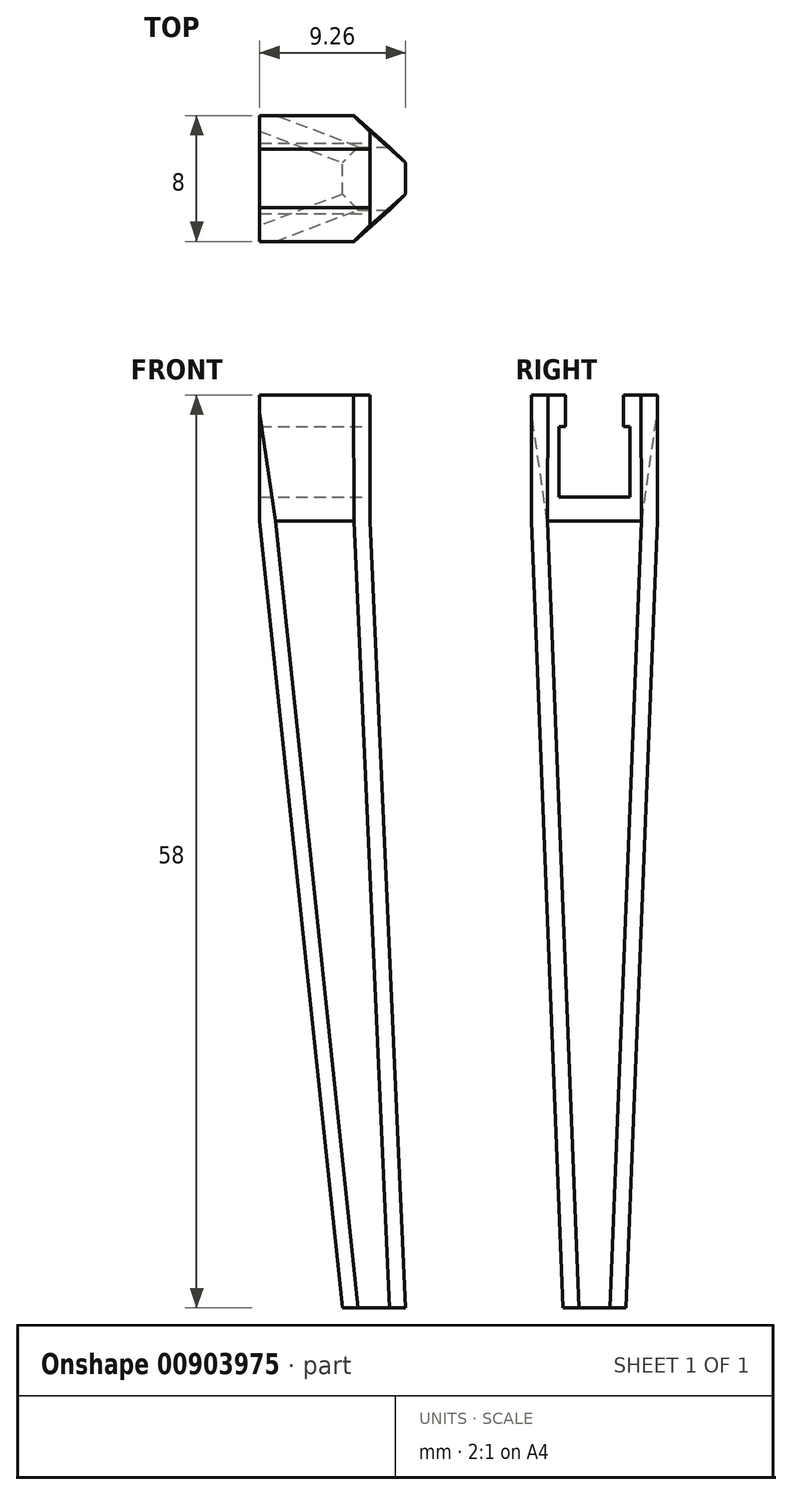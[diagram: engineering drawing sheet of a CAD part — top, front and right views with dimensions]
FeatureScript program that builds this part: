
annotation { "Feature Type Name" : "Feature", "Feature Type Description" : "" }
export const myFeature = defineFeature(function(context is Context, id is Id, definition is map)
    precondition{}
    {
        {
            var Q0;
            Q0=qCreatedBy(makeId("Front.planeOp"),FACE);
            var sketch = newSketch(context, id + "F0", { "sketchPlane" : qUnion([Q0])});
            skLineSegment(sketch, "E0", {"start": v(0, 0) * mm, "end": v(5.26, -50) * mm});
            skLineSegment(sketch, "E1", {"start": v(5.26, -50) * mm, "end": v(9.26, -50) * mm});
            skLineSegment(sketch, "E2", {"start": v(9.26, -50) * mm, "end": v(7, 0) * mm});
            skLineSegment(sketch, "E3", {"start": v(7, 0) * mm, "end": v(7, 8) * mm});
            skLineSegment(sketch, "E4", {"start": v(7, 8) * mm, "end": v(0, 8) * mm});
            skLineSegment(sketch, "E5", {"start": v(0, 8) * mm, "end": v(0, 0) * mm});
            skSolve(sketch);
        }
        {
            var Q0;
            Q0 = qSketchRegion(id + "F0", true);
            extrude(context, id + "F1", {"entities" : qUnion([Q0]), "endBound" : BoundingType.SYMMETRIC, "depth" : 8 * mm, "offsetDistance" : 25 * mm});
        }
        {
            var Q0;
            Q0=qCreatedBy(makeId("Right.planeOp"),FACE);
            var sketch = newSketch(context, id + "F2", { "sketchPlane" : qUnion([Q0])});
            skLineSegment(sketch, "E6", {"start": v(-2.25, 6) * mm, "end": v(-2.25, 1.5) * mm});
            skLineSegment(sketch, "E7", {"start": v(-2.25, 1.5) * mm, "end": v(2.25, 1.5) * mm});
            skLineSegment(sketch, "E8", {"start": v(2.25, 1.5) * mm, "end": v(2.25, 6) * mm});
            skLineSegment(sketch, "E9", {"start": v(2.25, 6) * mm, "end": v(1.85, 6) * mm});
            skLineSegment(sketch, "E10", {"start": v(1.85, 6) * mm, "end": v(1.85, 11) * mm});
            skLineSegment(sketch, "E11", {"start": v(1.85, 11) * mm, "end": v(-1.85, 11) * mm});
            skLineSegment(sketch, "E12", {"start": v(-1.85, 11) * mm, "end": v(-1.85, 6) * mm});
            skLineSegment(sketch, "E13", {"start": v(-1.85, 6) * mm, "end": v(-2.25, 6) * mm});
            skSolve(sketch);
        }
        {
            var Q0;
            Q0 = qSketchRegion(id + "F2", true);
            extrude(context, id + "F3", {"entities" : qUnion([Q0]), "operationType" : NewBodyOperationType.REMOVE, "endBound" : BoundingType.SYMMETRIC, "oppositeDirection" : true, "depth" : 25 * mm, "offsetDistance" : 25 * mm});
        }
        {
            var Q0;
            Q0=qCreatedBy(makeId("Right.planeOp"),FACE);
            var sketch = newSketch(context, id + "F4", { "sketchPlane" : qUnion([Q0])});
            skLineSegment(sketch, "E14", {"start": v(-4, 0) * mm, "end": v(-2, -50) * mm});
            skLineSegment(sketch, "E15", {"start": v(-2, -50) * mm, "end": v(-9.35, -50) * mm});
            skLineSegment(sketch, "E16", {"start": v(-9.35, -50) * mm, "end": v(-9.35, 0) * mm});
            skLineSegment(sketch, "E17", {"start": v(-9.35, 0) * mm, "end": v(-4, 0) * mm});
            skLineSegment(sketch, "E18.MirrorCS", {"start": v(9.35, 0) * mm, "end": v(4, 0) * mm});
            skLineSegment(sketch, "E19.MirrorCS", {"start": v(4, 0) * mm, "end": v(2, -50) * mm});
            skLineSegment(sketch, "E20.MirrorCS", {"start": v(9.35, -50) * mm, "end": v(9.35, 0) * mm});
            skLineSegment(sketch, "E21.MirrorCS", {"start": v(2, -50) * mm, "end": v(9.35, -50) * mm});
            skSolve(sketch);
        }
        {
            var Q0;
            Q0 = qSketchRegion(id + "F4", true);
            extrude(context, id + "F5", {"entities" : qUnion([Q0]), "operationType" : NewBodyOperationType.REMOVE, "endBound" : BoundingType.SYMMETRIC, "oppositeDirection" : true, "depth" : 25 * mm, "offsetDistance" : 25 * mm});
        }
        {
            var Q0;
            Q0=makeQuery(id+"F5.boolean.opBoolean","INTERSECT",EDGE,{"derivedFrom":[makeQuery(id+"F1.opExtrude","SWEPT_FACE",FACE,{"disambiguationData":[OSD([sQuery(id+"F0.wireOp",EDGE,"E2")])]}),makeQuery(id+"F5.opExtrude","SWEPT_FACE",FACE,{"disambiguationData":[OSD([sQuery(id+"F4.wireOp",EDGE,"E14")])]})]});
            var Q1;
            Q1=makeQuery(id+"F5.boolean.opBoolean","INTERSECT",EDGE,{"derivedFrom":[makeQuery(id+"F1.opExtrude","SWEPT_FACE",FACE,{"disambiguationData":[OSD([sQuery(id+"F0.wireOp",EDGE,"E0")])]}),makeQuery(id+"F5.opExtrude","SWEPT_FACE",FACE,{"disambiguationData":[OSD([sQuery(id+"F4.wireOp",EDGE,"E14")])]})]});
            var Q2;
            Q2=makeQuery(id+"F5.boolean.opBoolean","INTERSECT",EDGE,{"derivedFrom":[makeQuery(id+"F1.opExtrude","SWEPT_FACE",FACE,{"disambiguationData":[OSD([sQuery(id+"F0.wireOp",EDGE,"E0")])]}),makeQuery(id+"F5.opExtrude","SWEPT_FACE",FACE,{"disambiguationData":[OSD([sQuery(id+"F4.wireOp",EDGE,"E19.MirrorCS")])]})]});
            var Q3;
            Q3=makeQuery(id+"F5.boolean.opBoolean","INTERSECT",EDGE,{"derivedFrom":[makeQuery(id+"F1.opExtrude","SWEPT_FACE",FACE,{"disambiguationData":[OSD([sQuery(id+"F0.wireOp",EDGE,"E2")])]}),makeQuery(id+"F5.opExtrude","SWEPT_FACE",FACE,{"disambiguationData":[OSD([sQuery(id+"F4.wireOp",EDGE,"E19.MirrorCS")])]})]});
            chamfer(context, id + "F6", {"entities" : qUnion([Q0, Q1, Q2, Q3]), "width" : 1 * mm, "tangentPropagation" : true});
        }
    });
